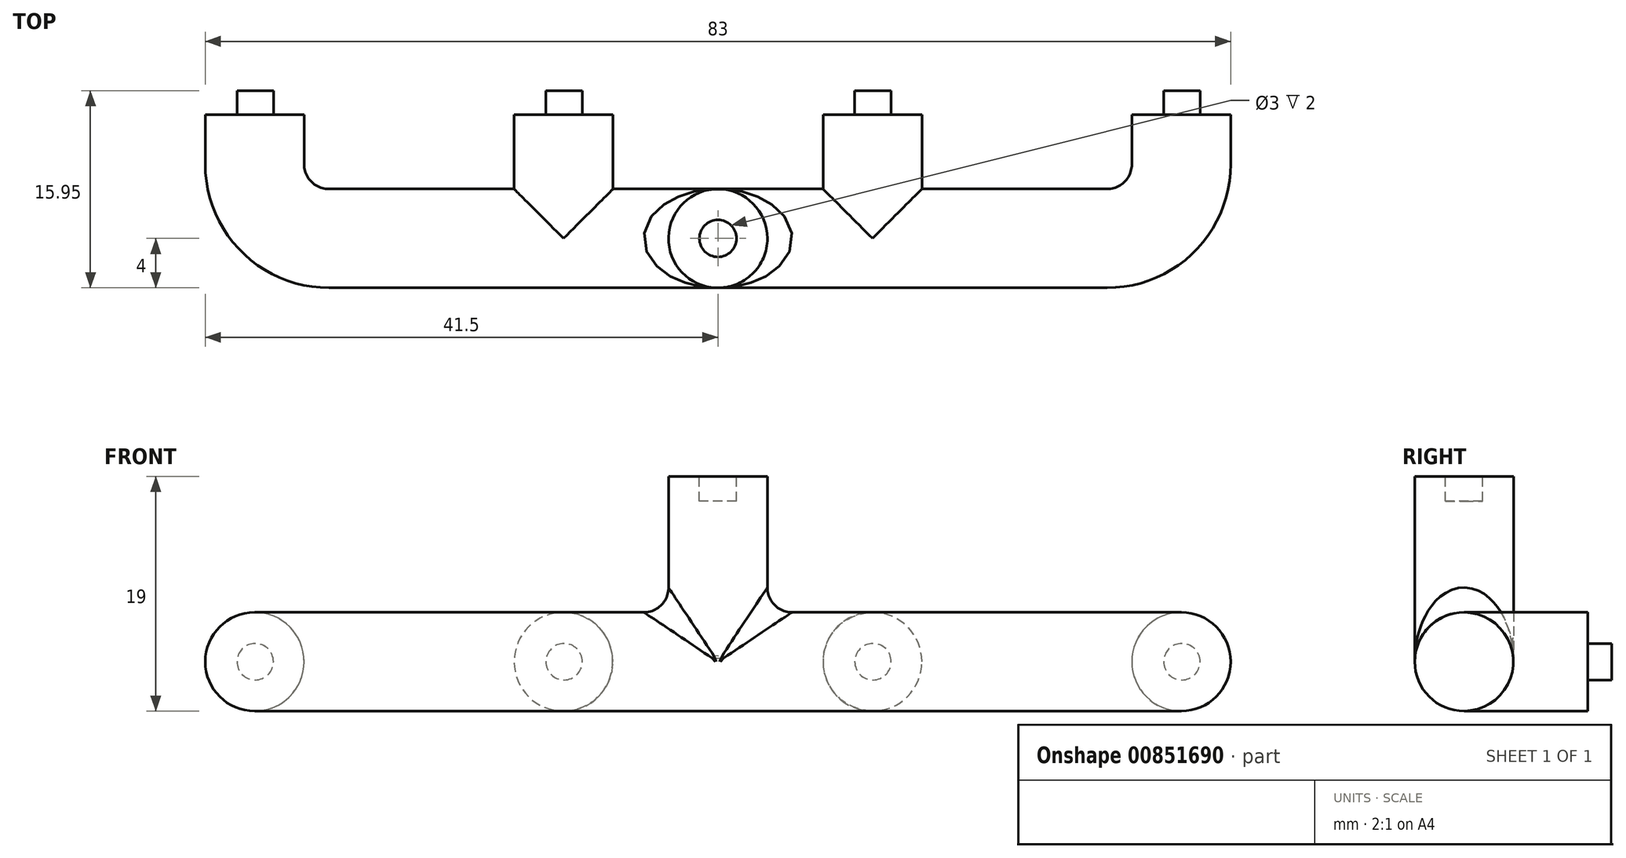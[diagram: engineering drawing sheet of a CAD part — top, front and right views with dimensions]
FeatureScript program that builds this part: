
annotation { "Feature Type Name" : "Feature", "Feature Type Description" : "" }
export const myFeature = defineFeature(function(context is Context, id is Id, definition is map)
    precondition{}
    {
        {
            var Q0;
            Q0=qCreatedBy(makeId("Top.planeOp"),FACE);
            var sketch = newSketch(context, id + "F0", { "sketchPlane" : qUnion([Q0])});
            skLineSegment(sketch, "E0", {"start": v(0, 0) * mm, "end": v(25, 0) * mm, "construction": true});
            skLineSegment(sketch, "E1", {"start": v(0, 0) * mm, "end": v(-25, 0) * mm, "construction": true});
            skLineSegment(sketch, "E2", {"start": v(-25, 0) * mm, "end": v(-50, 0) * mm, "construction": true});
            skLineSegment(sketch, "E3", {"start": v(-50, 0) * mm, "end": v(-50, -4) * mm});
            skLineSegment(sketch, "E4.1.0.0", {"start": v(-25, 0) * mm, "end": v(-25, -10) * mm});
            skLineSegment(sketch, "E4.2.0.0", {"start": v(0, 0) * mm, "end": v(0, -10) * mm});
            skLineSegment(sketch, "E4.3.0.0", {"start": v(25, 0) * mm, "end": v(25, -4) * mm});
            skLineSegment(sketch, "E4.direction1", {"start": v(-50, -10) * mm, "end": v(-25, -10) * mm, "construction": true});
            skLineSegment(sketch, "E5", {"start": v(-44, -10) * mm, "end": v(19, -10) * mm});
            skPoint(sketch, "E6.visualSharp", {"position": v(-50, -10) * mm});
            skArc(sketch, "E6.filletArc", {"start": v(-50, -4) * mm, "mid": v(-48.24, -8.24) * mm, "end": v(-44, -10) * mm});
            skPoint(sketch, "E7.visualSharp", {"position": v(25, -10) * mm});
            skArc(sketch, "E7.filletArc", {"start": v(19, -10) * mm, "mid": v(23.24, -8.24) * mm, "end": v(25, -4) * mm});
            skSolve(sketch);
        }
        {
            var Q0;
            Q0=qCreatedBy(makeId("Front.planeOp"),FACE);
            var sketch = newSketch(context, id + "F1", { "sketchPlane" : qUnion([Q0])});
            skCircle(sketch, "E8", {"center": v(-50, 0) * mm, "radius": 4 * mm});
            skCircle(sketch, "E9.1.0.0", {"center": v(-25, 0) * mm, "radius": 4 * mm});
            skCircle(sketch, "E9.2.0.0", {"center": v(0, 0) * mm, "radius": 4 * mm});
            skCircle(sketch, "E9.3.0.0", {"center": v(25, 0) * mm, "radius": 4 * mm});
            skLineSegment(sketch, "E9.direction1", {"start": v(-50, 0) * mm, "end": v(-25, 0) * mm, "construction": true});
            skSolve(sketch);
        }
        {
            var Q0;
            Q0=makeQuery(id+"F1.imprint","IMPRINT",FACE,{"disambiguationData":[TD([[makeQuery(id+"F1.imprint","IMPRINT",EDGE,{"derivedFrom":sQuery(id+"F1.wireOp",EDGE,"E8")}),1.0]])]});
            var Q1;
            Q1=sQuery(id+"F0.wireOp",EDGE,"E3");
            var Q2;
            Q2=sQuery(id+"F0.wireOp",EDGE,"E6.filletArc");
            var Q3;
            Q3=sQuery(id+"F0.wireOp",EDGE,"E5");
            var Q4;
            Q4=sQuery(id+"F0.wireOp",EDGE,"E7.filletArc");
            var Q5;
            Q5=sQuery(id+"F0.wireOp",EDGE,"E4.3.0.0");
            sweep(context, id + "F2", {"profiles" : qUnion([Q0]), "path" : qUnion([Q1, Q2, Q3, Q4, Q5])});
        }
        {
            var Q0;
            Q0=makeQuery(id+"F1.imprint","IMPRINT",FACE,{"disambiguationData":[TD([[makeQuery(id+"F1.imprint","IMPRINT",EDGE,{"derivedFrom":sQuery(id+"F1.wireOp",EDGE,"E9.1.0.0")}),1.0]])]});
            var Q1;
            Q1=makeQuery(id+"F1.imprint","IMPRINT",FACE,{"disambiguationData":[TD([[makeQuery(id+"F1.imprint","IMPRINT",EDGE,{"derivedFrom":sQuery(id+"F1.wireOp",EDGE,"E9.2.0.0")}),1.0]])]});
            var Q2;
            Q2=sQuery(id+"F0.wireOp",EDGE,"E4.1.0.0");
            sweep(context, id + "F3", {"operationType" : NewBodyOperationType.ADD, "profiles" : qUnion([Q0, Q1]), "path" : qUnion([Q2])});
        }
        {
            var Q0;
            Q0=makeQuery(id+"F1.imprint","IMPRINT",FACE,{"disambiguationData":[TD([[makeQuery(id+"F1.imprint","IMPRINT",EDGE,{"derivedFrom":sQuery(id+"F1.wireOp",EDGE,"E9.3.0.0")}),1.0]])]});
            var sketch = newSketch(context, id + "F4", { "sketchPlane" : qUnion([Q0])});
            skCircle(sketch, "E10", {"center": v(25.05, 0) * mm, "radius": 1.48 * mm});
            skCircle(sketch, "E11.1.0.0", {"center": v(0.05, 0) * mm, "radius": 1.48 * mm});
            skCircle(sketch, "E11.2.0.0", {"center": v(-24.95, 0) * mm, "radius": 1.48 * mm});
            skCircle(sketch, "E11.3.0.0", {"center": v(-49.95, 0) * mm, "radius": 1.48 * mm});
            skLineSegment(sketch, "E11.direction1", {"start": v(25.05, 0) * mm, "end": v(0.05, 0) * mm, "construction": true});
            skSolve(sketch);
        }
        {
            var Q0;
            Q0=makeQuery(id+"F4.imprint","IMPRINT",FACE,{"disambiguationData":[TD([[makeQuery(id+"F4.imprint","IMPRINT",EDGE,{"derivedFrom":sQuery(id+"F4.wireOp",EDGE,"E10")}),1.0]])]});
            var Q1;
            Q1=makeQuery(id+"F4.imprint","IMPRINT",FACE,{"disambiguationData":[TD([[makeQuery(id+"F4.imprint","IMPRINT",EDGE,{"derivedFrom":sQuery(id+"F4.wireOp",EDGE,"E11.1.0.0")}),1.0]])]});
            var Q2;
            Q2=makeQuery(id+"F4.imprint","IMPRINT",FACE,{"disambiguationData":[TD([[makeQuery(id+"F4.imprint","IMPRINT",EDGE,{"derivedFrom":sQuery(id+"F4.wireOp",EDGE,"E11.2.0.0")}),1.0]])]});
            var Q3;
            Q3=makeQuery(id+"F4.imprint","IMPRINT",FACE,{"disambiguationData":[TD([[makeQuery(id+"F4.imprint","IMPRINT",EDGE,{"derivedFrom":sQuery(id+"F4.wireOp",EDGE,"E11.3.0.0")}),1.0]])]});
            extrude(context, id + "F5", {"entities" : qUnion([Q0, Q1, Q2, Q3]), "operationType" : NewBodyOperationType.ADD, "depth" : -1.95 * mm, "offsetDistance" : 25 * mm});
        }
        {
            var Q0;
            Q0=qCreatedBy(makeId("Top.planeOp"),FACE);
            var sketch = newSketch(context, id + "F6", { "sketchPlane" : qUnion([Q0])});
            skCircle(sketch, "E12", {"center": v(-12.5, -10) * mm, "radius": 4 * mm});
            skSolve(sketch);
        }
        {
            var Q0;
            Q0 = qSketchRegion(id + "F6", true);
            extrude(context, id + "F7", {"entities" : qUnion([Q0]), "operationType" : NewBodyOperationType.ADD, "depth" : 15 * mm, "offsetDistance" : 25 * mm});
        }
        {
            var Q0;
            Q0=makeQuery(id+"F7.opExtrude","CAP_FACE",FACE,{"disambiguationData":[OSD([sQuery(id+"F6.wireOp",EDGE,"E12")])],"isStart":false});
            var sketch = newSketch(context, id + "F8", { "sketchPlane" : qUnion([Q0])});
            skLineSegment(sketch, "E13", {"start": v(-12.48, -14) * mm, "end": v(-12.48, -6) * mm, "construction": true});
            skLineSegment(sketch, "E14", {"start": v(-12.48, -6) * mm, "end": v(-12.5, -10) * mm, "construction": true});
            skLineSegment(sketch, "E15", {"start": v(-12.5, -10) * mm, "end": v(-9.76, -10.01) * mm, "construction": true});
            skCircle(sketch, "E16", {"center": v(-12.5, -10) * mm, "radius": 1.5 * mm});
            skSolve(sketch);
        }
        {
            var Q0;
            Q0=makeQuery(id+"F8.imprint","IMPRINT",FACE,{"disambiguationData":[TD([[makeQuery(id+"F8.imprint","IMPRINT",EDGE,{"derivedFrom":sQuery(id+"F8.wireOp",EDGE,"E16")}),1.0]])]});
            extrude(context, id + "F9", {"entities" : qUnion([Q0]), "operationType" : NewBodyOperationType.REMOVE, "oppositeDirection" : true, "depth" : 2 * mm, "offsetDistance" : 25 * mm});
        }
        {
            var Q0;
            Q0=makeQuery(id+"F7.boolean.opBoolean","INTERSECT",EDGE,{"derivedFrom":[makeQuery(id+"F2.opSweep","SWEPT_FACE",FACE,{"disambiguationData":[OSD([sQuery(id+"F0.wireOp",EDGE,"E5"),sQuery(id+"F1.wireOp",EDGE,"E8")])]}),makeQuery(id+"F7.opExtrude","SWEPT_FACE",FACE,{"disambiguationData":[OSD([sQuery(id+"F6.wireOp",EDGE,"E12")])]})]});
            fillet(context, id + "F10", {"entities" : qUnion([Q0]), "radius" : 2 * mm, "tangentPropagation" : true, "allowEdgeOverflow" : false});
        }
    });
